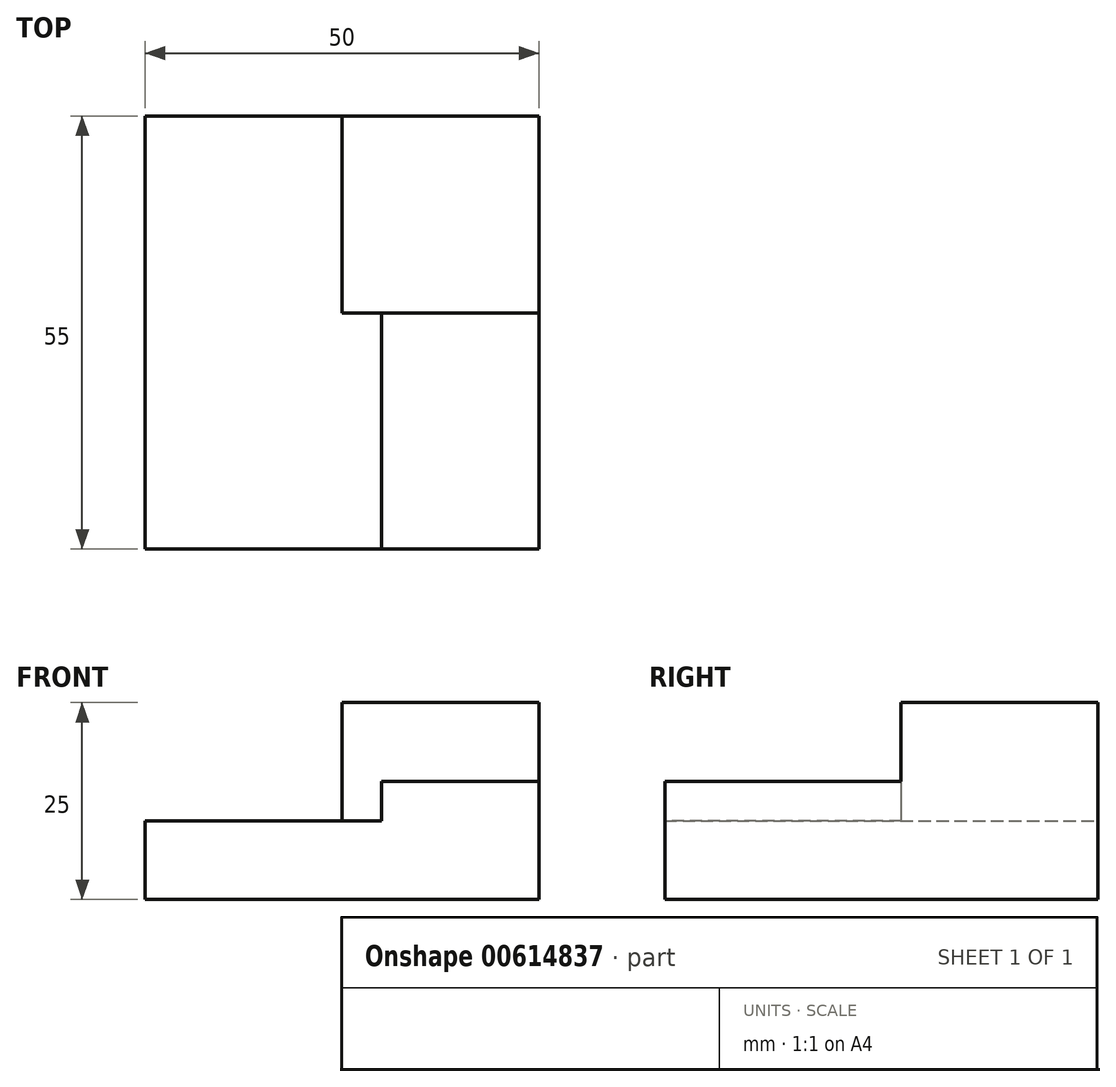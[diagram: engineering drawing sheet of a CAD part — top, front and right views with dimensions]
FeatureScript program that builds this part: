
annotation { "Feature Type Name" : "Feature", "Feature Type Description" : "" }
export const myFeature = defineFeature(function(context is Context, id is Id, definition is map)
    precondition{}
    {
        {
            var Q0;
            Q0=qCreatedBy(makeId("Top.planeOp"),FACE);
            var sketch = newSketch(context, id + "F0", { "sketchPlane" : qUnion([Q0])});
            skLineSegment(sketch, "E0", {"start": v(0, 0) * mm, "end": v(0, 25) * mm});
            skLineSegment(sketch, "E1", {"start": v(0, 25) * mm, "end": v(25, 25) * mm});
            skLineSegment(sketch, "E2", {"start": v(25, 25) * mm, "end": v(25, 0) * mm});
            skLineSegment(sketch, "E3", {"start": v(25, 0) * mm, "end": v(0, 0) * mm});
            skLineSegment(sketch, "E4", {"start": v(5, 0) * mm, "end": v(5, -30) * mm});
            skLineSegment(sketch, "E5", {"start": v(5, -30) * mm, "end": v(25, -30) * mm});
            skLineSegment(sketch, "E6", {"start": v(25, -30) * mm, "end": v(25, 0) * mm});
            skLineSegment(sketch, "E7", {"start": v(5, -30) * mm, "end": v(-25, -30) * mm});
            skLineSegment(sketch, "E8", {"start": v(-25, -30) * mm, "end": v(-25, 25) * mm});
            skLineSegment(sketch, "E9", {"start": v(-25, 25) * mm, "end": v(0, 25) * mm});
            skSolve(sketch);
        }
        {
            var Q0;
            {var subQ3=sQuery(id+"F0.wireOp",EDGE,"E0");Q0=makeQuery(id+"F0.imprint","IMPRINT",FACE,{"disambiguationData":[TD([[makeQuery(id+"F0.imprint","IMPRINT",EDGE,{"derivedFrom":subQ3}),-1.0]])]});}
            extrude(context, id + "F1", {"entities" : qUnion([Q0]), "depth" : 25 * mm, "offsetDistance" : 25.4 * mm});
        }
        {
            var Q0;
            {var subQ1=sQuery(id+"F0.wireOp",EDGE,"E0");Q0=makeQuery(id+"F0.imprint","IMPRINT",FACE,{"disambiguationData":[TD([[makeQuery(id+"F0.imprint","IMPRINT",EDGE,{"derivedFrom":subQ1}),1.0]])]});}
            extrude(context, id + "F2", {"entities" : qUnion([Q0]), "operationType" : NewBodyOperationType.ADD, "depth" : 10 * mm, "offsetDistance" : 25.4 * mm});
        }
        {
            var Q0;
            {var subQ2=sQuery(id+"F0.wireOp",EDGE,"E4");Q0=makeQuery(id+"F0.imprint","IMPRINT",FACE,{"disambiguationData":[TD([[makeQuery(id+"F0.imprint","IMPRINT",EDGE,{"derivedFrom":subQ2}),1.0]])]});}
            extrude(context, id + "F3", {"entities" : qUnion([Q0]), "operationType" : NewBodyOperationType.ADD, "depth" : 15 * mm, "offsetDistance" : 25.4 * mm});
        }
    });
